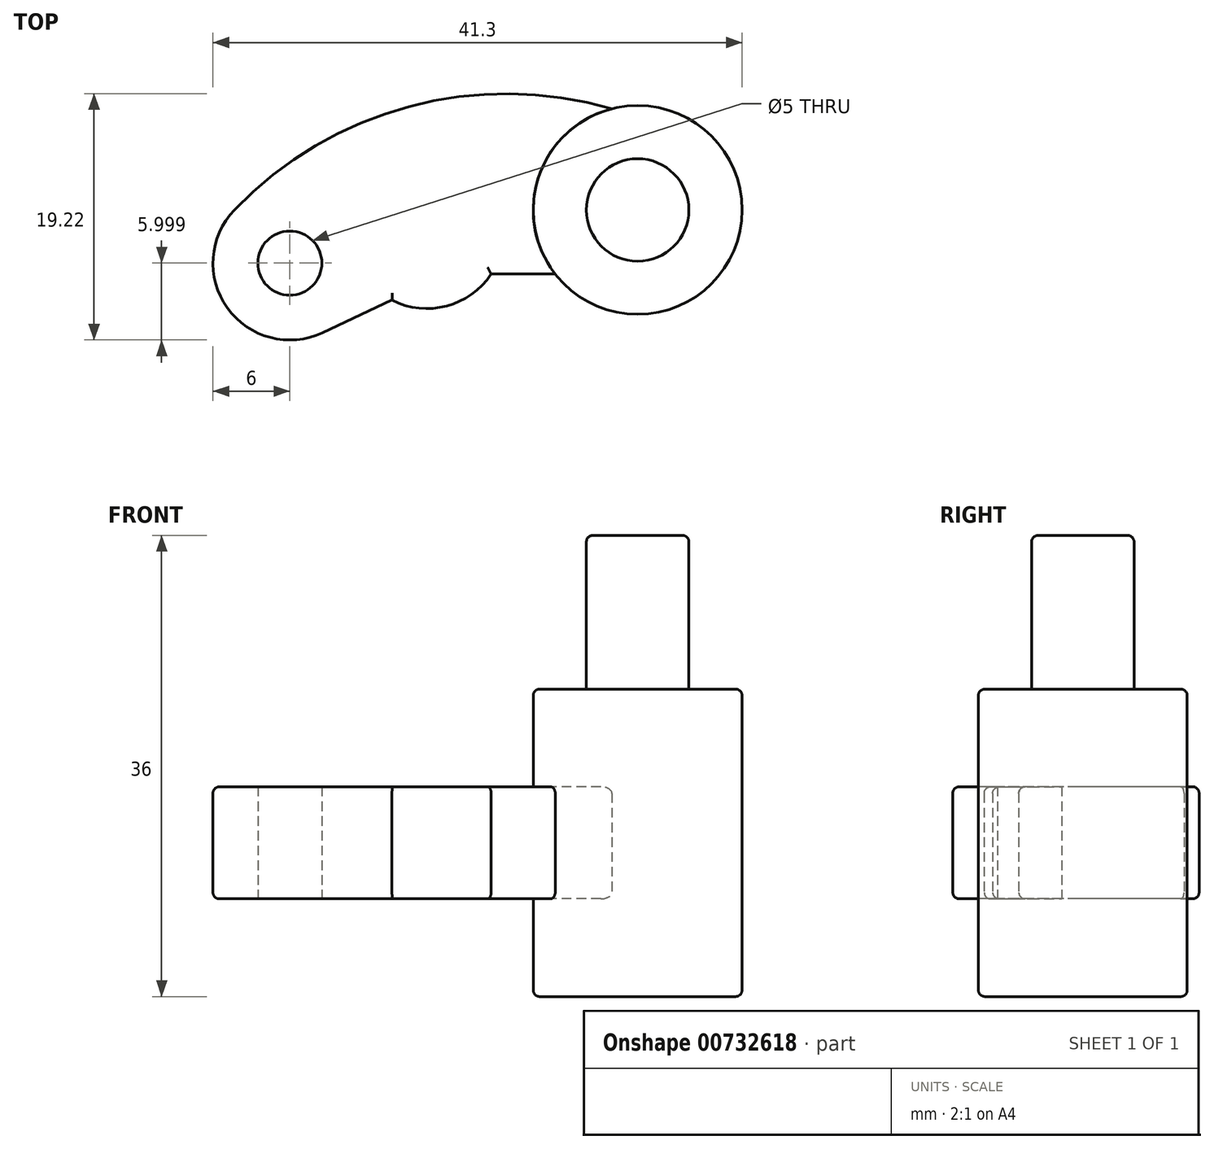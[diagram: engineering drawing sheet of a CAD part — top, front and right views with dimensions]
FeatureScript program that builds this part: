
annotation { "Feature Type Name" : "Feature", "Feature Type Description" : "" }
export const myFeature = defineFeature(function(context is Context, id is Id, definition is map)
    precondition{}
    {
        {
            var Q0;
            Q0=qCreatedBy(makeId("Top.planeOp"),FACE);
            var sketch = newSketch(context, id + "F0", { "sketchPlane" : qUnion([Q0])});
            skCircle(sketch, "E0", {"center": v(0, 0) * mm, "radius": 8.15 * mm});
            skLineSegment(sketch, "E1", {"start": v(-6.44, -5) * mm, "end": v(-11.44, -5) * mm});
            skPoint(sketch, "E2", {"position": v(-19.17, -7.04) * mm});
            skArc(sketch, "E3", {"start": v(-19.17, -7.04) * mm, "mid": v(-14.91, -7.5) * mm, "end": v(-11.44, -5) * mm});
            skLineSegment(sketch, "E4", {"start": v(-19.17, -7.04) * mm, "end": v(-24.6, -9.58) * mm});
            skArc(sketch, "E5", {"start": v(-31.48, 0) * mm, "mid": v(-32.02, -7.65) * mm, "end": v(-24.6, -9.58) * mm});
            skArc(sketch, "E6", {"start": v(-2, 7.9) * mm, "mid": v(-17.85, 8.07) * mm, "end": v(-31.48, 0) * mm});
            skLineSegment(sketch, "E7", {"start": v(-8.15, 9) * mm, "end": v(-8.15, -5) * mm, "construction": true});
            skLineSegment(sketch, "E8", {"start": v(-33.15, 4.16) * mm, "end": v(-33.15, -15.29) * mm, "construction": true});
            skCircle(sketch, "E9", {"center": v(-27.15, -4.15) * mm, "radius": 2.5 * mm});
            skSolve(sketch);
        }
        {
            var Q0;
            {var subQ0=sQuery(id+"F0.wireOp",EDGE,"E0");var subQ1=makeQuery(id+"F0.imprint","INTERSECT",VERTEX,{"derivedFrom":[subQ0,sQuery(id+"F0.wireOp",EDGE,"E1")]});Q0=makeQuery(id+"F0.imprint","IMPRINT",FACE,{"disambiguationData":[TD([[makeQuery(id+"F0.imprint","IMPRINT",EDGE,{"disambiguationData":[TD([[subQ1,1.0]])],"derivedFrom":subQ0}),1.0]])]});}
            extrude(context, id + "F1", {"entities" : qUnion([Q0]), "depth" : 12 * mm, "offsetDistance" : 25 * mm, "hasSecondDirection" : true, "secondDirectionOppositeDirection" : true, "secondDirectionDepth" : 12 * mm});
        }
        {
            var Q0;
            Q0=makeQuery(id+"F1.opExtrude","CAP_FACE",FACE,{"disambiguationData":[OSD([sQuery(id+"F0.wireOp",EDGE,"E0")])],"isStart":false});
            var sketch = newSketch(context, id + "F2", { "sketchPlane" : qUnion([Q0])});
            skCircle(sketch, "E10", {"center": v(0, 0) * mm, "radius": 4 * mm});
            skSolve(sketch);
        }
        {
            var Q0;
            Q0=makeQuery(id+"F2.imprint","IMPRINT",FACE,{"disambiguationData":[TD([[makeQuery(id+"F2.imprint","IMPRINT",EDGE,{"derivedFrom":sQuery(id+"F2.wireOp",EDGE,"E10")}),1.0]])]});
            var Q1;
            Q1=sQuery(id+"F2.wireOp",EDGE,"E10");
            extrude(context, id + "F3", {"entities" : qUnion([Q0]), "operationType" : NewBodyOperationType.ADD, "surfaceEntities" : qUnion([Q1]), "depth" : 12 * mm, "offsetDistance" : 25 * mm});
        }
        {
            var Q0;
            {var subQ0=sQuery(id+"F0.wireOp",EDGE,"E1");Q0=makeQuery(id+"F0.imprint","IMPRINT",FACE,{"disambiguationData":[TD([[makeQuery(id+"F0.imprint","IMPRINT",EDGE,{"derivedFrom":subQ0}),-1.0]])]});}
            extrude(context, id + "F4", {"entities" : qUnion([Q0]), "operationType" : NewBodyOperationType.ADD, "depth" : (8.75 / 2) * mm, "offsetDistance" : 25 * mm, "hasSecondDirection" : true, "secondDirectionOppositeDirection" : true, "secondDirectionDepth" : (8.75 / 2) * mm});
        }
        {
            var Q0;
            Q0=makeQuery(id+"F3.opExtrude","CAP_EDGE",EDGE,{"disambiguationData":[OSD([sQuery(id+"F2.wireOp",EDGE,"E10")])],"isStart":false});
            var Q1;
            Q1=makeQuery(id+"F1.opExtrude","CAP_EDGE",EDGE,{"disambiguationData":[OSD([sQuery(id+"F0.wireOp",EDGE,"E0")])],"isStart":false});
            var Q2;
            Q2=makeQuery(id+"F1.opExtrude","CAP_EDGE",EDGE,{"disambiguationData":[OSD([sQuery(id+"F0.wireOp",EDGE,"E0")])],"isStart":true});
            var Q3;
            Q3=makeQuery(id+"FqMvh81FxkIwgXG_1.1.F3.opExtrude","CAP_EDGE",EDGE,{"disambiguationData":[OSD([sQuery(id+"F2.wireOp",EDGE,"E10")])],"isStart":false});
            var Q4;
            Q4=makeQuery(id+"F4.opExtrude","CAP_EDGE",EDGE,{"disambiguationData":[OSD([sQuery(id+"F0.wireOp",EDGE,"E6")])],"isStart":false});
            var Q5;
            Q5=makeQuery(id+"F4.opExtrude","CAP_EDGE",EDGE,{"disambiguationData":[OSD([sQuery(id+"F0.wireOp",EDGE,"E6")])],"isStart":true});
            var Q6;
            Q6=makeQuery(id+"F4.opExtrude","CAP_EDGE",EDGE,{"disambiguationData":[OSD([sQuery(id+"F0.wireOp",EDGE,"E3")])],"isStart":false});
            var Q7;
            Q7=makeQuery(id+"F4.opExtrude","CAP_EDGE",EDGE,{"disambiguationData":[OSD([sQuery(id+"F0.wireOp",EDGE,"E1")])],"isStart":false});
            var Q8;
            Q8=makeQuery(id+"F4.opExtrude","CAP_EDGE",EDGE,{"disambiguationData":[OSD([sQuery(id+"F0.wireOp",EDGE,"E3")])],"isStart":true});
            var Q9;
            Q9=makeQuery(id+"F4.opExtrude","CAP_EDGE",EDGE,{"disambiguationData":[OSD([sQuery(id+"F0.wireOp",EDGE,"E1")])],"isStart":true});
            fillet(context, id + "F5", {"entities" : qUnion([Q0, Q1, Q2, Q3, Q4, Q5, Q6, Q7, Q8, Q9]), "radius" : .5 * mm, "tangentPropagation" : true, "allowEdgeOverflow" : false});
        }
    });
